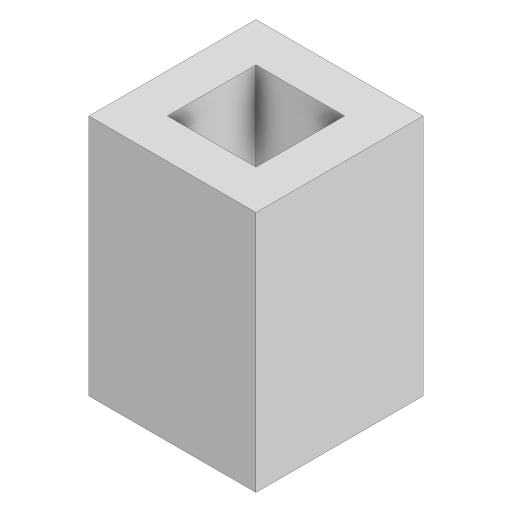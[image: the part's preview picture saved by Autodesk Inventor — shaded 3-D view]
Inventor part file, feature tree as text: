
AUTODESK INVENTOR PART (.ipt)
format: ipt  version: 2024.3 (Build 283343000, 343)  size: 350,720 bytes
history: native  units: mm
features: extrude x2, other x1, sketch x1
ambient origin geometry x8: Origin, YZ Plane, XZ Plane, XY Plane, X Axis, Y Axis, Z Axis, Center Point
bodies: Body1 (feature_tree)
feature tree (4):
  other  "Sólido1"
  sketch  "Esboço1"  dims[d0=6.0mm d1=6.0mm d2=6.0mm d3=6.0mm d4=13.5mm d5=13.5mm d6=3.0mm d7=0.0mm d8=37.0mm d9=0.0mm]
  extrude  "Extrusão1"  Depth=6.0mm
  extrude  "Extrusão2"  Depth=6.0mm
